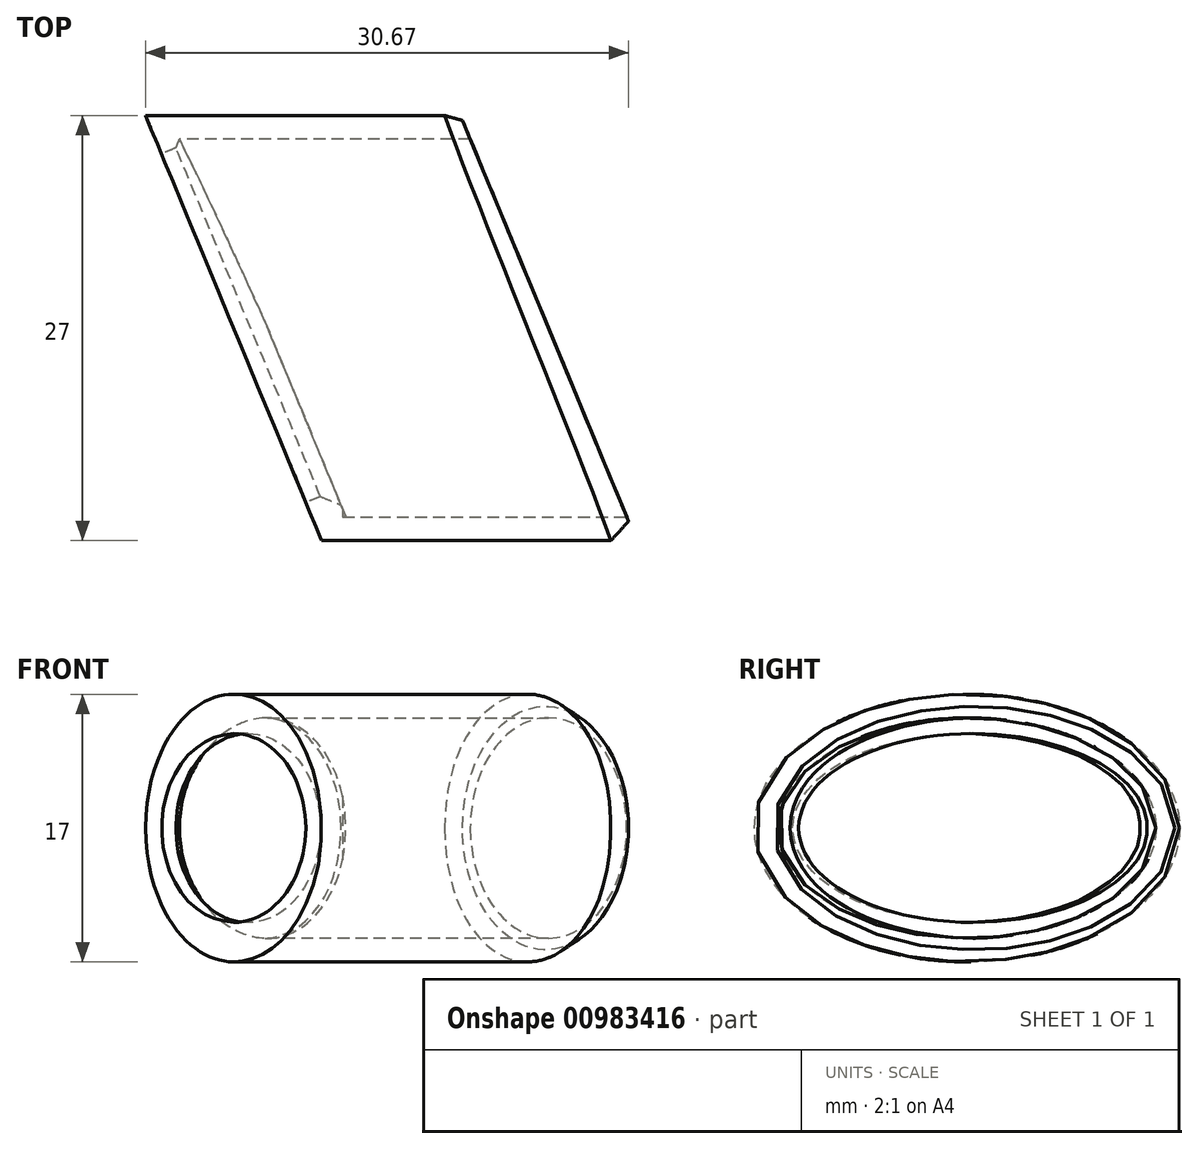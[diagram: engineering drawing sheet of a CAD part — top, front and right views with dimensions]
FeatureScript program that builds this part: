
annotation { "Feature Type Name" : "Feature", "Feature Type Description" : "" }
export const myFeature = defineFeature(function(context is Context, id is Id, definition is map)
    precondition{}
    {
        {
            var Q0;
            Q0=qCreatedBy(makeId("Right.planeOp"),FACE);
            var sketch = newSketch(context, id + "F0", { "sketchPlane" : qUnion([Q0])});
            skEllipse(sketch, "E0", {"center": v(-13.5, 0) * mm, "majorRadius": 12 * mm, "minorRadius": 7 * mm, "majorAxis": v(1, 0)});
            skEllipse(sketch, "E1", {"center": v(-13.5, 0) * mm, "majorRadius": 13.5 * mm, "minorRadius": 8.5 * mm, "majorAxis": v(1, 0)});
            skPoint(sketch, "E2", {"position": v(-27, 0) * mm});
            skPoint(sketch, "E3", {"position": v(-25.5, 0) * mm});
            skPoint(sketch, "E4", {"position": v(-13.5, 7) * mm});
            skPoint(sketch, "E5", {"position": v(-13.5, 8.5) * mm});
            skPoint(sketch, "E6", {"position": v(-13.5, -8.5) * mm});
            skPoint(sketch, "E7", {"position": v(0, 0) * mm});
            skSolve(sketch);
        }
        {
            var Q0;
            Q0 = qSketchRegion(id + "F0", true);
            extrude(context, id + "F1", {"entities" : qUnion([Q0]), "depth" : 50 * mm, "offsetDistance" : 25 * mm});
        }
        {
            var Q0;
            Q0=qCreatedBy(makeId("Top.planeOp"),FACE);
            var sketch = newSketch(context, id + "F2", { "sketchPlane" : qUnion([Q0])});
            skLineSegment(sketch, "E8", {"start": v(0, 0) * mm, "end": v(12.43, -30) * mm});
            skLineSegment(sketch, "E9", {"start": v(12.43, -30) * mm, "end": v(0, -30) * mm});
            skLineSegment(sketch, "E10", {"start": v(0, -30) * mm, "end": v(0, 0) * mm});
            skLineSegment(sketch, "E11", {"start": v(0, 0) * mm, "end": v(20, 0) * mm, "construction": true});
            skLineSegment(sketch, "E12", {"start": v(20, 0) * mm, "end": v(32.43, -30) * mm});
            skLineSegment(sketch, "E13", {"start": v(32.43, -30) * mm, "end": v(12.43, -30) * mm, "construction": true});
            skLineSegment(sketch, "E14", {"start": v(20, 0) * mm, "end": v(60, 0) * mm});
            skLineSegment(sketch, "E15", {"start": v(60, 0) * mm, "end": v(60, -30) * mm});
            skLineSegment(sketch, "E16", {"start": v(60, -30) * mm, "end": v(32.43, -30) * mm});
            skSolve(sketch);
        }
        {
            var Q0;
            Q0 = qSketchRegion(id + "F2", true);
            extrude(context, id + "F3", {"entities" : qUnion([Q0]), "operationType" : NewBodyOperationType.REMOVE, "endBound" : BoundingType.SYMMETRIC, "oppositeDirection" : true, "depth" : 25 * mm, "offsetDistance" : 25 * mm});
        }
        {
            var Q0;
            Q0=makeQuery(id+"F3.boolean.opBoolean","INTERSECT",EDGE,{"derivedFrom":[makeQuery(id+"F1.opExtrude","SWEPT_FACE",FACE,{"disambiguationData":[OSD([sQuery(id+"F0.wireOp",EDGE,"E1")])]}),makeQuery(id+"F3.opExtrude","SWEPT_FACE",FACE,{"disambiguationData":[OSD([sQuery(id+"F2.wireOp",EDGE,"E12")])]})]});
            chamfer(context, id + "F4", {"entities" : qUnion([Q0]), "chamferType" : ChamferType.OFFSET_ANGLE, "width" : 1 * mm, "oppositeDirection" : false, "angle" : 15 * degree, "tangentPropagation" : true});
        }
        {
            var Q0;
            Q0=makeQuery(id+"F3.boolean.opBoolean","COPY",FACE,{"derivedFrom":makeQuery(id+"F3.opExtrude","SWEPT_FACE",FACE,{"disambiguationData":[OSD([sQuery(id+"F2.wireOp",EDGE,"E8")])]})});
            var sketch = newSketch(context, id + "F5", { "sketchPlane" : qUnion([Q0])});
            skEllipse(sketch, "E17", {"center": v(14.61, 0) * mm, "majorRadius": 11.99 * mm, "minorRadius": 6 * mm, "majorAxis": v(1, 0)});
            skLineSegment(sketch, "E18", {"start": v(1.62, 0) * mm, "end": v(2.62, 0) * mm, "construction": true});
            skLineSegment(sketch, "E19", {"start": v(26.6, 0) * mm, "end": v(27.6, 0) * mm, "construction": true});
            skLineSegment(sketch, "E20", {"start": v(14.61, 7) * mm, "end": v(14.61, 6) * mm, "construction": true});
            skLineSegment(sketch, "E21", {"start": v(14.61, 6) * mm, "end": v(14.61, 0) * mm, "construction": true});
            skLineSegment(sketch, "E22", {"start": v(14.61, -6) * mm, "end": v(14.61, 0) * mm, "construction": true});
            skLineSegment(sketch, "E23", {"start": v(14.61, -6) * mm, "end": v(14.61, -7) * mm, "construction": true});
            skEllipse(sketch, "E24", {"center": v(14.61, 0) * mm, "majorRadius": 13.74 * mm, "minorRadius": 7.75 * mm, "majorAxis": v(1, 0)});
            skLineSegment(sketch, "E25", {"start": v(14.61, 7) * mm, "end": v(14.61, 7.75) * mm, "construction": true});
            skLineSegment(sketch, "E26", {"start": v(27.6, 0) * mm, "end": v(28.35, 0) * mm, "construction": true});
            skSolve(sketch);
        }
        {
            var Q0;
            Q0 = qSketchRegion(id + "F5", true);
            extrude(context, id + "F6", {"entities" : qUnion([Q0]), "operationType" : NewBodyOperationType.ADD, "depth" : -2 * mm, "offsetDistance" : 25 * mm});
        }
        {
            var Q0;
            Q0=makeQuery(id+"F6.opExtrude","CAP_EDGE",EDGE,{"disambiguationData":[OSD([sQuery(id+"F5.wireOp",EDGE,"E17")])],"isStart":false});
            chamfer(context, id + "F7", {"entities" : qUnion([Q0]), "width" : 1 * mm, "tangentPropagation" : true});
        }
    });
